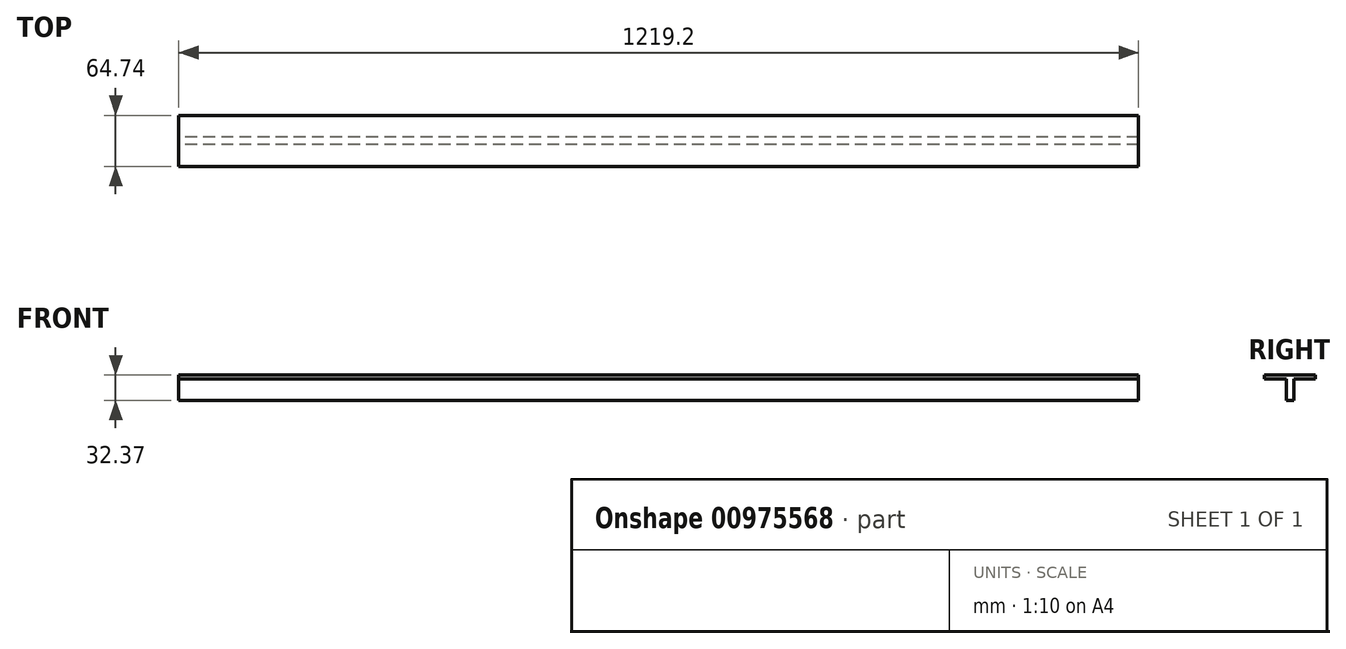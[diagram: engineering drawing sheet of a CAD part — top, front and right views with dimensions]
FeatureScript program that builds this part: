
annotation { "Feature Type Name" : "Feature", "Feature Type Description" : "" }
export const myFeature = defineFeature(function(context is Context, id is Id, definition is map)
    precondition{}
    {
        {
            var Q0;
            Q0=qCreatedBy(makeId("Right.planeOp"),FACE);
            var sketch = newSketch(context, id + "F0", { "sketchPlane" : qUnion([Q0])});
            skLineSegment(sketch, "E0.bottom", {"start": v(0, 0) * mm, "end": v(-32.37, 0) * mm});
            skLineSegment(sketch, "E0.left", {"start": v(0, 0) * mm, "end": v(0, -32.37) * mm});
            skLineSegment(sketch, "E1.top", {"start": v(-32.37, -4.77) * mm, "end": v(-4.77, -4.77) * mm});
            skLineSegment(sketch, "E1.right", {"start": v(-4.77, -32.37) * mm, "end": v(-4.77, -4.77) * mm});
            skLineSegment(sketch, "E2", {"start": v(0, -32.37) * mm, "end": v(-4.77, -32.37) * mm});
            skLineSegment(sketch, "E3", {"start": v(-32.37, 0) * mm, "end": v(-32.37, -4.77) * mm});
            skLineSegment(sketch, "E4.MirrorCS", {"start": v(32.37, 0) * mm, "end": v(32.37, -4.77) * mm});
            skLineSegment(sketch, "E5.MirrorCS", {"start": v(0, -32.37) * mm, "end": v(4.77, -32.37) * mm});
            skLineSegment(sketch, "E6.MirrorCS", {"start": v(4.77, -32.37) * mm, "end": v(4.77, -4.77) * mm});
            skLineSegment(sketch, "E7.MirrorCS", {"start": v(32.37, -4.77) * mm, "end": v(4.77, -4.77) * mm});
            skLineSegment(sketch, "E8.MirrorCS", {"start": v(0, 0) * mm, "end": v(32.37, 0) * mm});
            skSolve(sketch);
        }
        {
            var Q0;
            Q0 = qSketchRegion(id + "F0", true);
            extrude(context, id + "F1", {"entities" : qUnion([Q0]), "depth" : 1219.2 * mm, "offsetDistance" : 25.4 * mm});
        }
    });
